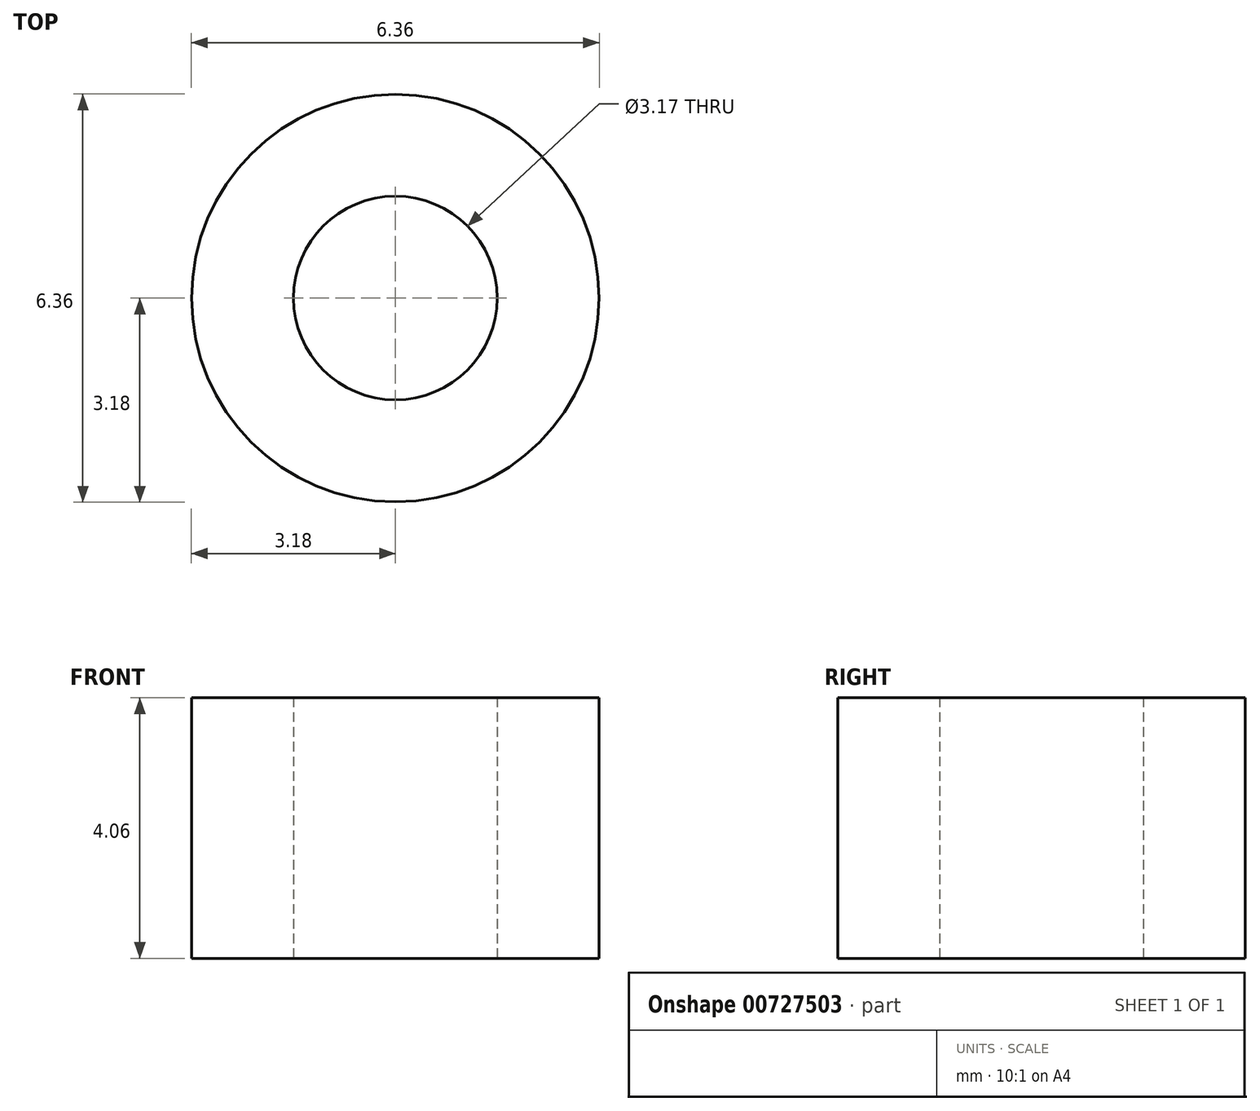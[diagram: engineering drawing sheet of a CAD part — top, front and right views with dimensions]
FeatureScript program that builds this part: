
annotation { "Feature Type Name" : "Feature", "Feature Type Description" : "" }
export const myFeature = defineFeature(function(context is Context, id is Id, definition is map)
    precondition{}
    {
        {
            var Q0;
            Q0=qCreatedBy(makeId("Top.planeOp"),FACE);
            var sketch = newSketch(context, id + "F0", { "sketchPlane" : qUnion([Q0])});
            skCircle(sketch, "E0", {"center": v(0, 0) * mm, "radius": 1.59 * mm});
            skCircle(sketch, "E1", {"center": v(0, 0) * mm, "radius": 3.18 * mm});
            skSolve(sketch);
        }
        {
            var Q0;
            Q0=makeQuery(id+"F0.imprint","IMPRINT",FACE,{"disambiguationData":[TD([[makeQuery(id+"F0.imprint","IMPRINT",EDGE,{"derivedFrom":sQuery(id+"F0.wireOp",EDGE,"E0")}),-1.0]])]});
            extrude(context, id + "F1", {"entities" : qUnion([Q0]), "depth" : 4.06 * mm, "offsetDistance" : 25.4 * mm});
        }
    });
